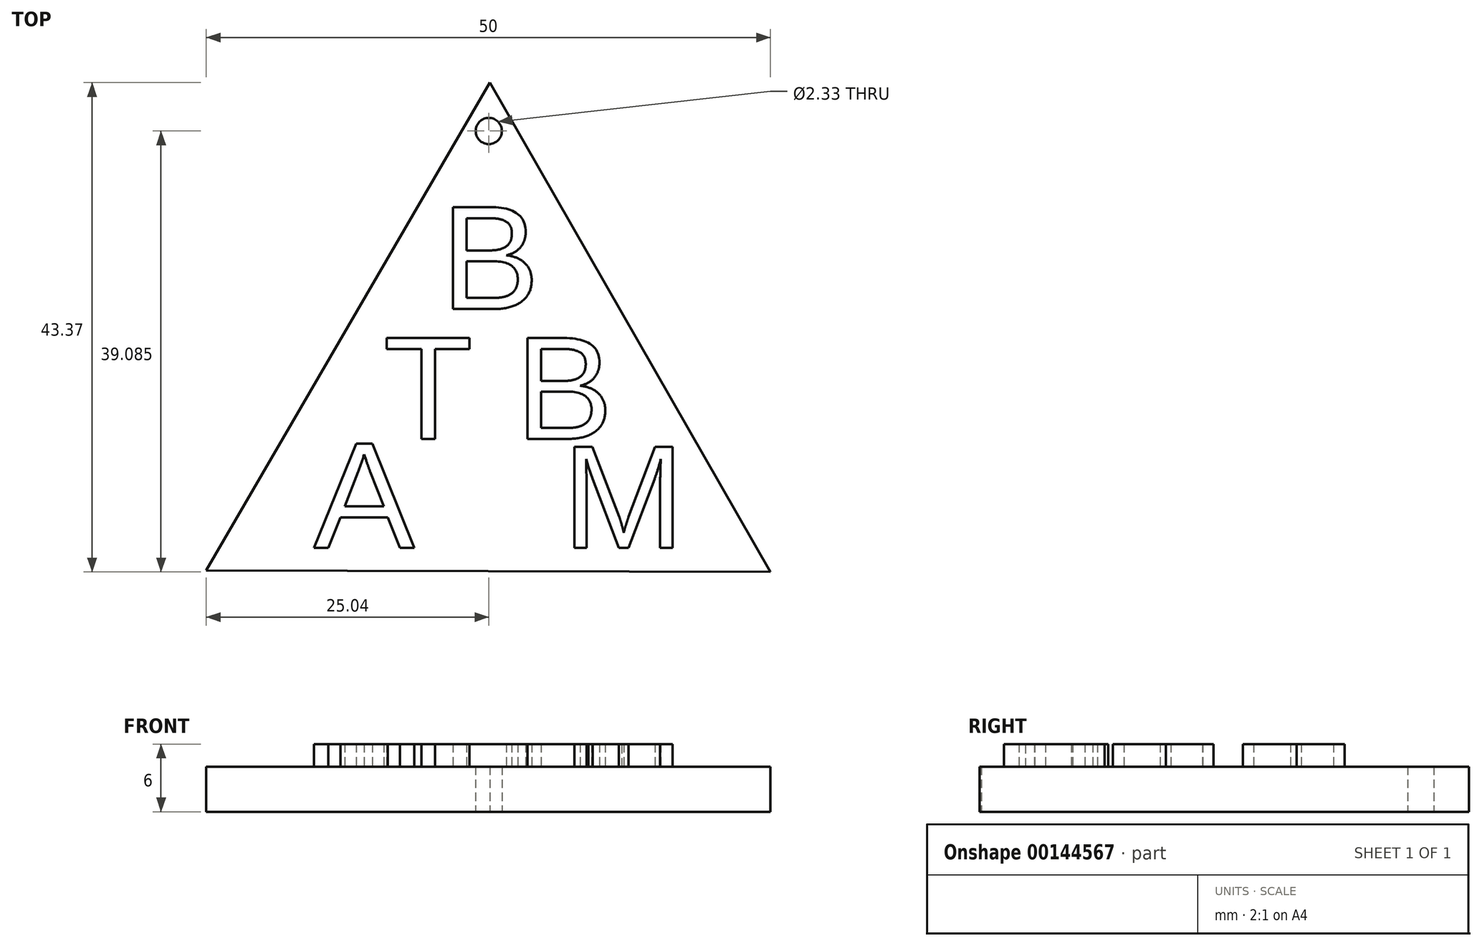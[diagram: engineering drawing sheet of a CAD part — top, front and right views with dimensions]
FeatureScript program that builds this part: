
annotation { "Feature Type Name" : "Feature", "Feature Type Description" : "" }
export const myFeature = defineFeature(function(context is Context, id is Id, definition is map)
    precondition{}
    {
        {
            var Q0;
            Q0=qCreatedBy(makeId("Top.planeOp"),FACE);
            var sketch = newSketch(context, id + "F0", { "sketchPlane" : qUnion([Q0])});
            skLineSegment(sketch, "E0.0", {"start": v(-25.04, -20.5) * mm, "end": v(0.08, 22.72) * mm});
            skLineSegment(sketch, "E0.1", {"start": v(0.08, 22.72) * mm, "end": v(24.96, -20.65) * mm});
            skLineSegment(sketch, "E0.2", {"start": v(24.96, -20.65) * mm, "end": v(-25.04, -20.5) * mm});
            skCircle(sketch, "E1", {"center": v(0, 18.44) * mm, "radius": 1.16 * mm});
            skSolve(sketch);
        }
        {
            var Q0;
            Q0=qCreatedBy(makeId("Top.planeOp"),FACE);
            var sketch = newSketch(context, id + "F1", { "sketchPlane" : qUnion([Q0])});
            skText(sketch, "E2", { "text": "B", "fontName": "Arimo-Regular.ttf"});
            skText(sketch, "E3", { "text": "T", "fontName": "Arimo-Regular.ttf"});
            skText(sketch, "E4", { "text": "B", "fontName": "Arimo-Regular.ttf"});
            skText(sketch, "E5", { "text": "A", "fontName": "Arimo-Regular.ttf"});
            skText(sketch, "E6", { "text": "M", "fontName": "Arimo-Regular.ttf"});
            const initialGuessF1  = {"E2": [-0.00426, 0.00266, 1, 0, 0.00945], "E3": [-0.00934, -0.00885, 1, 0, 0.00935], "E4": [0.00235, -0.00885, 1, 0, 0.00935], "E5": [-0.01553, -0.0185, 1, 0, 0.00966], "E6": [0.00653, -0.0185, 1, 0, 0.00935]};
            skSetInitialGuess(sketch, initialGuessF1);
            skSolve(sketch);
        }
        {
            var Q0;
            Q0 = qSketchRegion(id + "F0", true);
            extrude(context, id + "F2", {"entities" : qUnion([Q0]), "depth" : 4 * mm});
        }
        {
            var Q0;
            Q0 = qSketchRegion(id + "F1", true);
            extrude(context, id + "F3", {"entities" : qUnion([Q0]), "operationType" : NewBodyOperationType.ADD, "depth" : 6 * mm});
        }
    });
